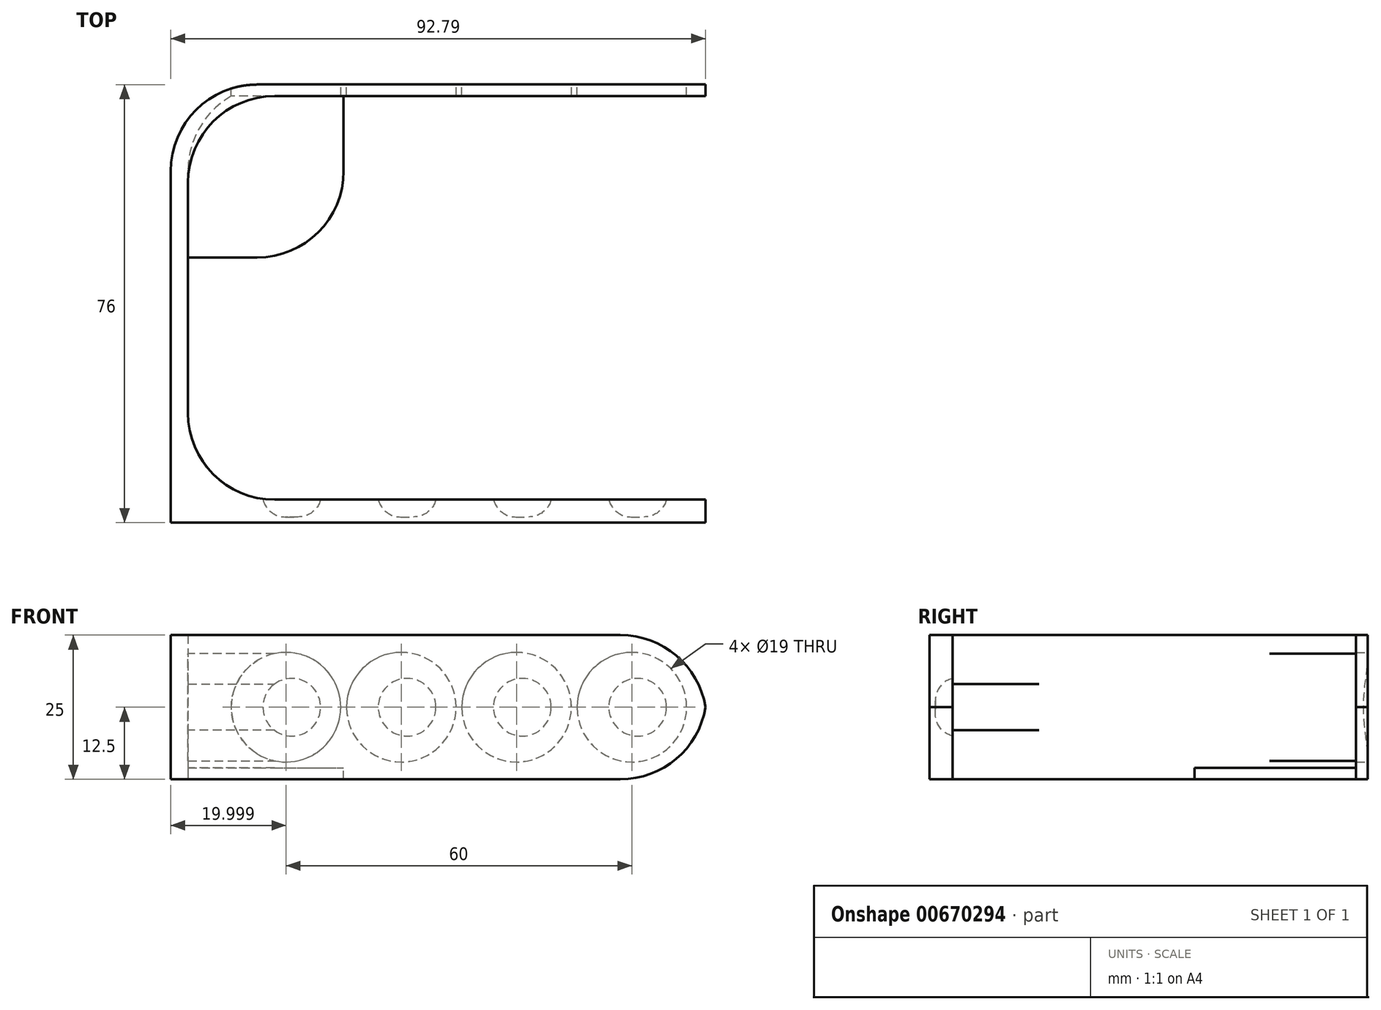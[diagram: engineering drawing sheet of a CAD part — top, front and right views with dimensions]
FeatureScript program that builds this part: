
annotation { "Feature Type Name" : "Feature", "Feature Type Description" : "" }
export const myFeature = defineFeature(function(context is Context, id is Id, definition is map)
    precondition{}
    {
        {
            var Q0;
            Q0=qCreatedBy(makeId("Top.planeOp"),FACE);
            var sketch = newSketch(context, id + "F0", { "sketchPlane" : qUnion([Q0])});
            skLineSegment(sketch, "E0", {"start": v(20.69, -48.9) * mm, "end": v(-69.31, -48.9) * mm});
            skLineSegment(sketch, "E1", {"start": v(20.69, -48.9) * mm, "end": v(20.69, -52.9) * mm});
            skLineSegment(sketch, "E2", {"start": v(20.69, -52.9) * mm, "end": v(-69.31, -52.9) * mm});
            skLineSegment(sketch, "E3", {"start": v(-69.31, -52.9) * mm, "end": v(-72.31, -52.9) * mm});
            skLineSegment(sketch, "E4", {"start": v(-72.31, -52.9) * mm, "end": v(-72.31, -48.9) * mm});
            skLineSegment(sketch, "E5", {"start": v(-69.31, 21.1) * mm, "end": v(20.69, 21.1) * mm});
            skLineSegment(sketch, "E6", {"start": v(20.69, 21.1) * mm, "end": v(20.69, 23.1) * mm});
            skLineSegment(sketch, "E7", {"start": v(20.69, 23.1) * mm, "end": v(-69.31, 23.1) * mm});
            skLineSegment(sketch, "E8", {"start": v(-69.31, 23.1) * mm, "end": v(-72.31, 23.1) * mm});
            skLineSegment(sketch, "E9", {"start": v(-69.31, -48.9) * mm, "end": v(-69.31, 21.1) * mm});
            skLineSegment(sketch, "E10", {"start": v(-72.31, 23.1) * mm, "end": v(-72.31, -48.9) * mm});
            skLineSegment(sketch, "E11.bottom", {"start": v(-69.31, 21.1) * mm, "end": v(-69.31, 21.1) * mm});
            skLineSegment(sketch, "E11.top", {"start": v(-69.31, 23.1) * mm, "end": v(-69.31, 23.1) * mm});
            skLineSegment(sketch, "E11.left", {"start": v(-69.31, 21.1) * mm, "end": v(-69.31, 23.1) * mm});
            skLineSegment(sketch, "E11.right", {"start": v(-69.31, 21.1) * mm, "end": v(-69.31, 23.1) * mm});
            skLineSegment(sketch, "E12.bottom", {"start": v(-69.31, -48.9) * mm, "end": v(-69.31, -48.9) * mm});
            skLineSegment(sketch, "E12.top", {"start": v(-69.31, -52.9) * mm, "end": v(-69.31, -52.9) * mm});
            skLineSegment(sketch, "E12.left", {"start": v(-69.31, -48.9) * mm, "end": v(-69.31, -52.9) * mm});
            skLineSegment(sketch, "E12.right", {"start": v(-69.31, -48.9) * mm, "end": v(-69.31, -52.9) * mm});
            skSolve(sketch);
        }
        {
            var Q0;
            Q0=makeQuery(id+"F0.imprint","IMPRINT",FACE,{"disambiguationData":[TD([[makeQuery(id+"F0.imprint","IMPRINT",EDGE,{"derivedFrom":sQuery(id+"F0.wireOp",EDGE,"E0")}),1.0]])]});
            var Q1;
            Q1=makeQuery(id+"F0.imprint","IMPRINT",FACE,{"disambiguationData":[TD([[makeQuery(id+"F0.imprint","IMPRINT",EDGE,{"derivedFrom":sQuery(id+"F0.wireOp",EDGE,"E3")}),-1.0]])]});
            var Q2;
            Q2=makeQuery(id+"F0.imprint","IMPRINT",FACE,{"disambiguationData":[TD([[makeQuery(id+"F0.imprint","IMPRINT",EDGE,{"derivedFrom":sQuery(id+"F0.wireOp",EDGE,"E5")}),1.0]])]});
            extrude(context, id + "F1", {"entities" : qUnion([Q0, Q1, Q2]), "endBound" : BoundingType.SYMMETRIC, "depth" : 25 * mm, "offsetDistance" : 25 * mm});
        }
        {
            var Q0;
            Q0=makeQuery(id+"F1.opExtrude","SWEPT_FACE",FACE,{"disambiguationData":[OSD([sQuery(id+"F0.wireOp",EDGE,"E7"),sQuery(id+"F0.wireOp",EDGE,"E8")])]});
            var sketch = newSketch(context, id + "F2", { "sketchPlane" : qUnion([Q0])});
            skCircle(sketch, "E13", {"center": v(52.31, 0) * mm, "radius": 9.5 * mm});
            skCircle(sketch, "E14", {"center": v(32.31, 0) * mm, "radius": 9.5 * mm});
            skCircle(sketch, "E15", {"center": v(12.31, 0) * mm, "radius": 9.5 * mm});
            skCircle(sketch, "E16", {"center": v(-7.69, 0) * mm, "radius": 9.5 * mm});
            skSolve(sketch);
        }
        {
            var Q0;
            Q0=makeQuery(id+"F2.imprint","IMPRINT",FACE,{"disambiguationData":[TD([[makeQuery(id+"F2.imprint","IMPRINT",EDGE,{"derivedFrom":sQuery(id+"F2.wireOp",EDGE,"E16")}),1.0]])]});
            var Q1;
            Q1=makeQuery(id+"F2.imprint","IMPRINT",FACE,{"disambiguationData":[TD([[makeQuery(id+"F2.imprint","IMPRINT",EDGE,{"derivedFrom":sQuery(id+"F2.wireOp",EDGE,"E15")}),1.0]])]});
            var Q2;
            Q2=makeQuery(id+"F2.imprint","IMPRINT",FACE,{"disambiguationData":[TD([[makeQuery(id+"F2.imprint","IMPRINT",EDGE,{"derivedFrom":sQuery(id+"F2.wireOp",EDGE,"E14")}),1.0]])]});
            var Q3;
            Q3=makeQuery(id+"F2.imprint","IMPRINT",FACE,{"disambiguationData":[TD([[makeQuery(id+"F2.imprint","IMPRINT",EDGE,{"derivedFrom":sQuery(id+"F2.wireOp",EDGE,"E13")}),1.0]])]});
            extrude(context, id + "F3", {"entities" : qUnion([Q0, Q1, Q2, Q3]), "operationType" : NewBodyOperationType.REMOVE, "oppositeDirection" : true, "depth" : 25 * mm, "offsetDistance" : 25 * mm});
        }
        {
            var Q0;
            Q0=makeQuery(id+"F1.opExtrude","SWEPT_FACE",FACE,{"disambiguationData":[OSD([sQuery(id+"F0.wireOp",EDGE,"E0")])]});
            var sketch = newSketch(context, id + "F4", { "sketchPlane" : qUnion([Q0])});
            skCircle(sketch, "E17", {"center": v(-8.69, 0) * mm, "radius": 5 * mm});
            skCircle(sketch, "E18", {"center": v(11.31, 0) * mm, "radius": 5 * mm});
            skCircle(sketch, "E19", {"center": v(31.31, 0) * mm, "radius": 5 * mm});
            skCircle(sketch, "E20", {"center": v(51.31, 0) * mm, "radius": 5 * mm});
            skSolve(sketch);
        }
        {
            var Q0;
            Q0=makeQuery(id+"F4.imprint","IMPRINT",FACE,{"disambiguationData":[TD([[makeQuery(id+"F4.imprint","IMPRINT",EDGE,{"derivedFrom":sQuery(id+"F4.wireOp",EDGE,"E17")}),1.0]])]});
            var Q1;
            Q1=makeQuery(id+"F4.imprint","IMPRINT",FACE,{"disambiguationData":[TD([[makeQuery(id+"F4.imprint","IMPRINT",EDGE,{"derivedFrom":sQuery(id+"F4.wireOp",EDGE,"E18")}),1.0]])]});
            var Q2;
            Q2=makeQuery(id+"F4.imprint","IMPRINT",FACE,{"disambiguationData":[TD([[makeQuery(id+"F4.imprint","IMPRINT",EDGE,{"derivedFrom":sQuery(id+"F4.wireOp",EDGE,"E19")}),1.0]])]});
            var Q3;
            Q3=makeQuery(id+"F4.imprint","IMPRINT",FACE,{"disambiguationData":[TD([[makeQuery(id+"F4.imprint","IMPRINT",EDGE,{"derivedFrom":sQuery(id+"F4.wireOp",EDGE,"E20")}),1.0]])]});
            extrude(context, id + "F5", {"entities" : qUnion([Q0, Q1, Q2, Q3]), "operationType" : NewBodyOperationType.REMOVE, "oppositeDirection" : true, "depth" : 3 * mm, "offsetDistance" : 25 * mm});
        }
        {
            var Q0;
            Q0=makeQuery(id+"F1.opExtrude","CAP_EDGE",EDGE,{"disambiguationData":[OSD([sQuery(id+"F0.wireOp",EDGE,"E6")])],"isStart":true});
            var Q1;
            Q1=makeQuery(id+"F1.opExtrude","CAP_EDGE",EDGE,{"disambiguationData":[OSD([sQuery(id+"F0.wireOp",EDGE,"E6")])],"isStart":false});
            var Q2;
            Q2=makeQuery(id+"F1.opExtrude","CAP_EDGE",EDGE,{"disambiguationData":[OSD([sQuery(id+"F0.wireOp",EDGE,"E1")])],"isStart":true});
            var Q3;
            Q3=makeQuery(id+"F1.opExtrude","CAP_EDGE",EDGE,{"disambiguationData":[OSD([sQuery(id+"F0.wireOp",EDGE,"E1")])],"isStart":false});
            fillet(context, id + "F6", {"entities" : qUnion([Q0, Q1, Q2, Q3]), "radius" : 15 * mm, "tangentPropagation" : true, "allowEdgeOverflow" : false});
        }
        {
            var Q0;
            Q0=makeQuery(id+"F1.opExtrude","SWEPT_EDGE",EDGE,{"disambiguationData":[OSD([sQuery(id+"F0.wireOp",EDGE,"E5"),sQuery(id+"F0.wireOp",EDGE,"E9")])]});
            var Q1;
            Q1=makeQuery(id+"F1.opExtrude","SWEPT_EDGE",EDGE,{"disambiguationData":[OSD([sQuery(id+"F0.wireOp",EDGE,"E0"),sQuery(id+"F0.wireOp",EDGE,"E9")])]});
            fillet(context, id + "F7", {"entities" : qUnion([Q0, Q1]), "radius" : 15 * mm, "tangentPropagation" : true, "allowEdgeOverflow" : false});
        }
        {
            var Q0;
            Q0=makeQuery(id+"F1.opExtrude","SWEPT_EDGE",EDGE,{"disambiguationData":[OSD([sQuery(id+"F0.wireOp",EDGE,"E8"),sQuery(id+"F0.wireOp",EDGE,"E10")])]});
            fillet(context, id + "F8", {"entities" : qUnion([Q0]), "radius" : 15 * mm, "tangentPropagation" : true, "allowEdgeOverflow" : false});
        }
        {
            var Q0;
            Q0=makeQuery(id+"F5.boolean.opBoolean","COPY",EDGE,{"derivedFrom":makeQuery(id+"F5.opExtrude","CAP_EDGE",EDGE,{"disambiguationData":[OSD([sQuery(id+"F4.wireOp",EDGE,"E20")])],"isStart":false})});
            var Q1;
            Q1=makeQuery(id+"F5.boolean.opBoolean","COPY",EDGE,{"derivedFrom":makeQuery(id+"F5.opExtrude","CAP_EDGE",EDGE,{"disambiguationData":[OSD([sQuery(id+"F4.wireOp",EDGE,"E19")])],"isStart":false})});
            var Q2;
            Q2=makeQuery(id+"F5.boolean.opBoolean","COPY",EDGE,{"derivedFrom":makeQuery(id+"F5.opExtrude","CAP_EDGE",EDGE,{"disambiguationData":[OSD([sQuery(id+"F4.wireOp",EDGE,"E18")])],"isStart":false})});
            var Q3;
            Q3=makeQuery(id+"F5.boolean.opBoolean","COPY",EDGE,{"derivedFrom":makeQuery(id+"F5.opExtrude","CAP_EDGE",EDGE,{"disambiguationData":[OSD([sQuery(id+"F4.wireOp",EDGE,"E17")])],"isStart":false})});
            fillet(context, id + "F9", {"entities" : qUnion([Q0, Q1, Q2, Q3]), "radius" : 4 * mm, "tangentPropagation" : true, "allowEdgeOverflow" : false});
        }
        {
            var Q0;
            Q0=qCreatedBy(makeId("Top.planeOp"),FACE);
            cPlane(context, id + "F10", {"entities" : qUnion([Q0]), "cplaneType" : CPlaneType.OFFSET, "offset" : 12.5 * mm, "oppositeDirection" : true, "width" : 150 * mm, "height" : 150 * mm});
        }
        {
            var Q0;
            Q0=qCreatedBy(id+"F10.planeOp",FACE);
            var sketch = newSketch(context, id + "F11", { "sketchPlane" : qUnion([Q0])});
            skLineSegment(sketch, "E21", {"start": v(-72.31, -6.9) * mm, "end": v(-42.31, -6.9) * mm});
            skLineSegment(sketch, "E22", {"start": v(-42.31, -6.9) * mm, "end": v(-42.31, 23.1) * mm});
            skLineSegment(sketch, "E23", {"start": v(-42.31, 23.1) * mm, "end": v(-72.31, 23.1) * mm});
            skLineSegment(sketch, "E24", {"start": v(-72.31, 23.1) * mm, "end": v(-72.31, -6.9) * mm});
            skCircle(sketch, "E25", {"center": v(-57.31, 8.1) * mm, "radius": 15 * mm});
            skSolve(sketch);
        }
        {
            var Q0;
            {var subQ0=sQuery(id+"F11.wireOp",EDGE,"E24");var subQ1=sQuery(id+"F11.wireOp",EDGE,"E21");var subQ2=makeQuery(id+"F11.imprint","INTERSECT",VERTEX,{"derivedFrom":[subQ1,subQ0]});Q0=makeQuery(id+"F11.imprint","IMPRINT",FACE,{"disambiguationData":[TD([[makeQuery(id+"F11.imprint","IMPRINT",EDGE,{"disambiguationData":[TD([[subQ2,-1.0]])],"derivedFrom":subQ1}),1.0]])]});}
            var Q1;
            {var subQ0=sQuery(id+"F11.wireOp",EDGE,"E25");var subQ1=makeQuery(id+"F11.imprint","INTERSECT",VERTEX,{"derivedFrom":[sQuery(id+"F11.wireOp",EDGE,"E22"),subQ0]});Q1=makeQuery(id+"F11.imprint","IMPRINT",FACE,{"disambiguationData":[TD([[makeQuery(id+"F11.imprint","IMPRINT",EDGE,{"disambiguationData":[TD([[subQ1,-1.0]])],"derivedFrom":subQ0}),1.0]])]});}
            var Q2;
            {var subQ0=sQuery(id+"F11.wireOp",EDGE,"E23");var subQ1=sQuery(id+"F11.wireOp",EDGE,"E22");var subQ2=makeQuery(id+"F11.imprint","INTERSECT",VERTEX,{"derivedFrom":[subQ1,subQ0]});Q2=makeQuery(id+"F11.imprint","IMPRINT",FACE,{"disambiguationData":[TD([[makeQuery(id+"F11.imprint","IMPRINT",EDGE,{"disambiguationData":[TD([[subQ2,1.0]])],"derivedFrom":subQ1}),1.0]])]});}
            extrude(context, id + "F12", {"entities" : qUnion([Q0, Q1, Q2]), "operationType" : NewBodyOperationType.ADD, "depth" : 2 * mm, "offsetDistance" : 25 * mm});
        }
    });
